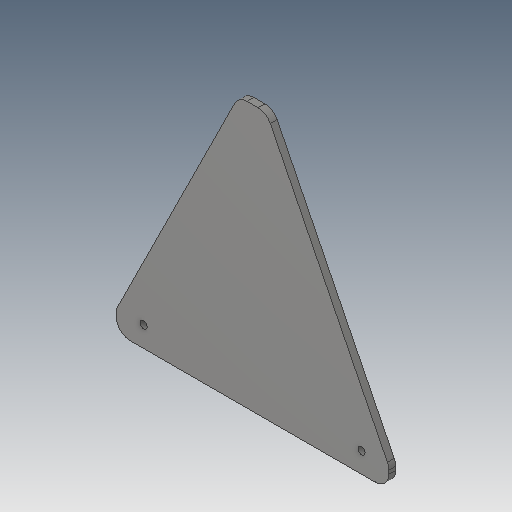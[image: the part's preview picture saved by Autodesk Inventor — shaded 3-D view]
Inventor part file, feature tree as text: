
AUTODESK INVENTOR PART (.ipt)
format: ipt  version: 2023.5 (Build 275446000, 446)  size: 94,720 bytes
history: native  units: in
note: dims shown in document units (in); Inventor stores cm internally (conversion verified against a paired STEP export)
features: fillet x1
ambient origin geometry x8: Origin, YZ Plane, XZ Plane, XY Plane, X Axis, Y Axis, Z Axis, Center Point
bodies: Solid1 (feature_tree)
feature tree (1):
  fillet  "Fillet2"  [1 undecoded]
note: 1 required parameter value undecoded (feature->parameter linkage not recoverable at this tier; creation-order binding heuristic only, values carry confidence <= 0.55)
